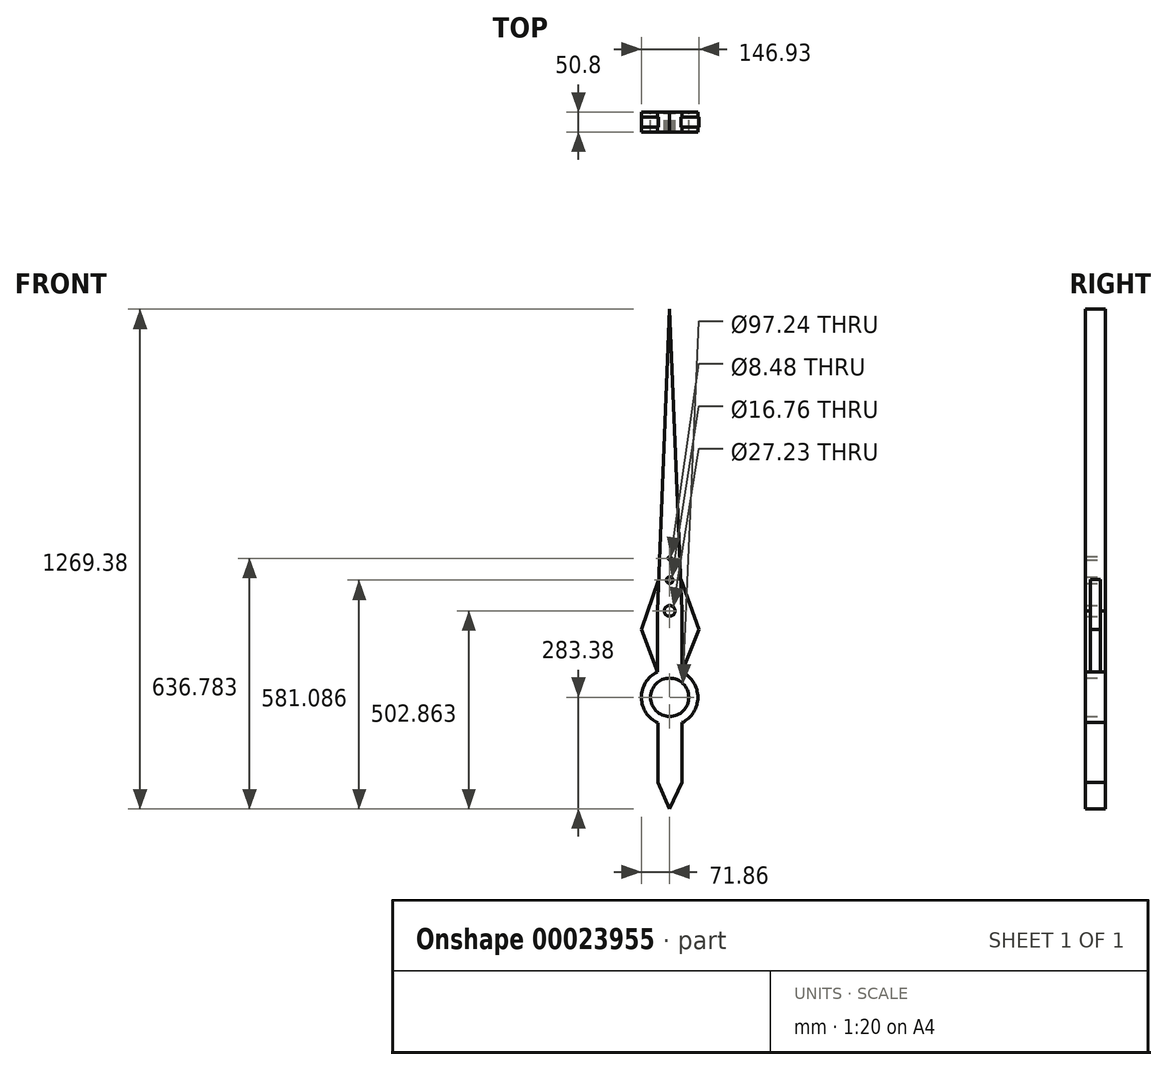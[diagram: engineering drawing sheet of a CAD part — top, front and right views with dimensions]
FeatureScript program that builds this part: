
annotation { "Feature Type Name" : "Feature", "Feature Type Description" : "" }
export const myFeature = defineFeature(function(context is Context, id is Id, definition is map)
    precondition{}
    {
        {
            var Q0;
            Q0=qCreatedBy(makeId("Front.planeOp"),FACE);
            var sketch = newSketch(context, id + "F0", { "sketchPlane" : qUnion([Q0])});
            skCircle(sketch, "E0", {"center": v(0, 0) * mm, "radius": 71.6 * mm});
            skLineSegment(sketch, "E1", {"start": v(-29.66, -65.17) * mm, "end": v(-29.66, -216.7) * mm});
            skLineSegment(sketch, "E2", {"start": v(31.5, -64.3) * mm, "end": v(31.5, -216.7) * mm});
            skLineSegment(sketch, "E3", {"start": v(-29.66, -216.7) * mm, "end": v(0, -283.38) * mm});
            skLineSegment(sketch, "E4", {"start": v(0, -283.38) * mm, "end": v(31.5, -216.7) * mm});
            skLineSegment(sketch, "E5", {"start": v(31.5, 64.3) * mm, "end": v(31.5, 219.48) * mm});
            skLineSegment(sketch, "E6", {"start": v(-31.5, 64.3) * mm, "end": v(-31.5, 219.48) * mm});
            skLineSegment(sketch, "E7", {"start": v(-31.5, 219.48) * mm, "end": v(0, 986) * mm});
            skLineSegment(sketch, "E8", {"start": v(0, 986) * mm, "end": v(31.5, 219.48) * mm});
            skCircle(sketch, "E9", {"center": v(0, 0) * mm, "radius": 48.62 * mm});
            skCircle(sketch, "E10", {"center": v(0, 219.48) * mm, "radius": 13.61 * mm});
            skCircle(sketch, "E11", {"center": v(0, 297.7) * mm, "radius": 8.38 * mm});
            skPoint(sketch, "E12.center.orphan", {"position": v(0, 353.4) * mm});
            skCircle(sketch, "E13", {"center": v(0, 353.4) * mm, "radius": 4.24 * mm});
            skLineSegment(sketch, "E14", {"start": v(0, 71.6) * mm, "end": v(0, 986) * mm});
            skLineSegment(sketch, "E15", {"start": v(28.23, 298.96) * mm, "end": v(75.07, 172.9) * mm});
            skLineSegment(sketch, "E16", {"start": v(75.07, 172.9) * mm, "end": v(31.5, 64.3) * mm});
            skLineSegment(sketch, "E17", {"start": v(-31.5, 64.3) * mm, "end": v(-71.86, 172.9) * mm});
            skLineSegment(sketch, "E18", {"start": v(-71.86, 172.9) * mm, "end": v(-28.28, 297.7) * mm});
            skSolve(sketch);
        }
        {
            var Q0;
            {var subQ1=sQuery(id+"F0.wireOp",EDGE,"E1");Q0=makeQuery(id+"F0.imprint","IMPRINT",FACE,{"disambiguationData":[TD([[makeQuery(id+"F0.imprint","IMPRINT",EDGE,{"derivedFrom":subQ1}),1.0]])]});}
            extrude(context, id + "F1", {"entities" : qUnion([Q0]), "endBound" : BoundingType.SYMMETRIC, "depth" : 50.8 * mm});
        }
        {
            var Q0;
            Q0=makeQuery(id+"F0.imprint","IMPRINT",FACE,{"disambiguationData":[TD([[makeQuery(id+"F0.imprint","IMPRINT",EDGE,{"derivedFrom":sQuery(id+"F0.wireOp",EDGE,"E9")}),-1.0]])]});
            extrude(context, id + "F2", {"entities" : qUnion([Q0]), "operationType" : NewBodyOperationType.ADD, "endBound" : BoundingType.SYMMETRIC, "depth" : 50.8 * mm});
        }
        {
            var Q0;
            {var subQ1=sQuery(id+"F0.wireOp",EDGE,"E5");Q0=makeQuery(id+"F0.imprint","IMPRINT",FACE,{"disambiguationData":[TD([[makeQuery(id+"F0.imprint","IMPRINT",EDGE,{"derivedFrom":subQ1}),1.0]])]});}
            extrude(context, id + "F3", {"entities" : qUnion([Q0]), "operationType" : NewBodyOperationType.ADD, "endBound" : BoundingType.SYMMETRIC, "depth" : 50.8 * mm});
        }
        {
            var Q0;
            {var subQ13=sQuery(id+"F0.wireOp",EDGE,"E6");Q0=makeQuery(id+"F0.imprint","IMPRINT",FACE,{"disambiguationData":[TD([[makeQuery(id+"F0.imprint","IMPRINT",EDGE,{"derivedFrom":subQ13}),-1.0]])]});}
            extrude(context, id + "F4", {"entities" : qUnion([Q0]), "operationType" : NewBodyOperationType.ADD, "endBound" : BoundingType.SYMMETRIC, "depth" : 50.8 * mm});
        }
        {
            var Q0;
            {var subQ2=sQuery(id+"F0.wireOp",EDGE,"E6");Q0=makeQuery(id+"F0.imprint","IMPRINT",FACE,{"disambiguationData":[TD([[makeQuery(id+"F0.imprint","IMPRINT",EDGE,{"derivedFrom":subQ2}),1.0]])]});}
            var Q1;
            {var subQ2=sQuery(id+"F0.wireOp",EDGE,"E5");Q1=makeQuery(id+"F0.imprint","IMPRINT",FACE,{"disambiguationData":[TD([[makeQuery(id+"F0.imprint","IMPRINT",EDGE,{"derivedFrom":subQ2}),-1.0]])]});}
            extrude(context, id + "F5", {"entities" : qUnion([Q0, Q1]), "operationType" : NewBodyOperationType.ADD, "endBound" : BoundingType.SYMMETRIC, "depth" : 25.4 * mm});
        }
    });
